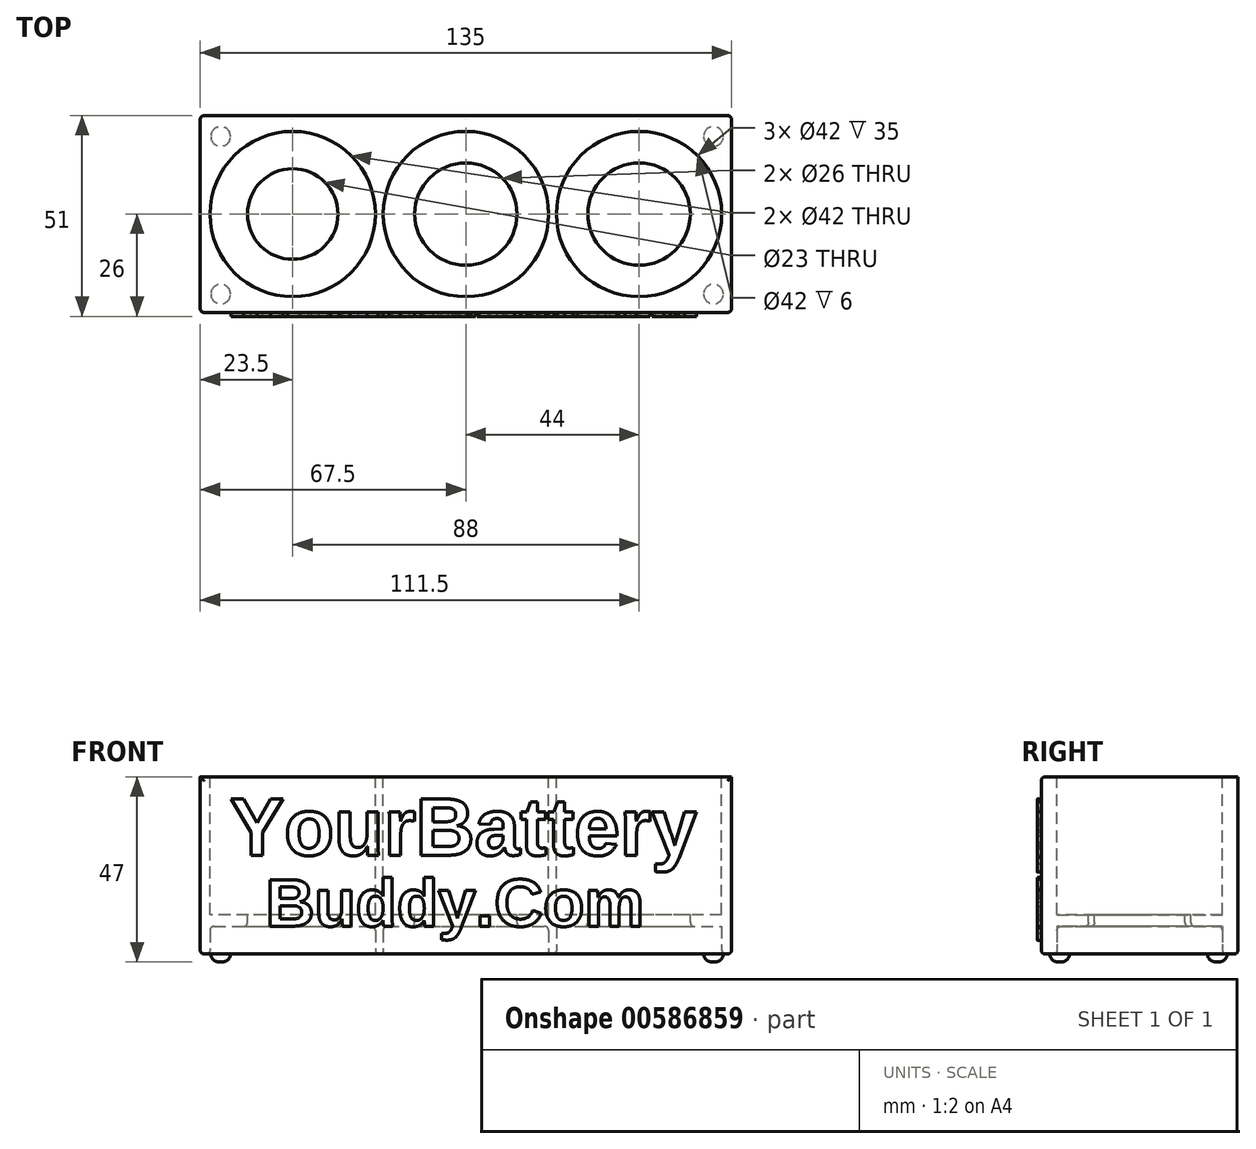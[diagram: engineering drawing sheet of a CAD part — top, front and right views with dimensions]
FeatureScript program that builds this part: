
annotation { "Feature Type Name" : "Feature", "Feature Type Description" : "" }
export const myFeature = defineFeature(function(context is Context, id is Id, definition is map)
    precondition{}
    {
        {
            var Q0;
            Q0=qCreatedBy(makeId("Top.planeOp"),FACE);
            var sketch = newSketch(context, id + "F0", { "sketchPlane" : qUnion([Q0])});
            skLineSegment(sketch, "E0.bottom", {"start": v(-67.5, -25) * mm, "end": v(67.5, -25) * mm});
            skLineSegment(sketch, "E0.top", {"start": v(-67.5, 25) * mm, "end": v(67.5, 25) * mm});
            skLineSegment(sketch, "E0.left", {"start": v(-67.5, -25) * mm, "end": v(-67.5, 25) * mm});
            skLineSegment(sketch, "E0.right", {"start": v(67.5, -25) * mm, "end": v(67.5, 25) * mm});
            skPoint(sketch, "E0.middle", {"position": v(0, 0) * mm});
            skSolve(sketch);
        }
        {
            var Q0;
            Q0 = qSketchRegion(id + "F0", true);
            extrude(context, id + "F1", {"entities" : qUnion([Q0]), "endBound" : BoundingType.SYMMETRIC, "depth" : 45 * mm, "offsetDistance" : 25 * mm});
        }
        {
            var Q0;
            Q0=makeQuery(id+"F1.opExtrude","CAP_FACE",FACE,{"disambiguationData":[OSD([sQuery(id+"F0.wireOp",EDGE,"E0.bottom"),sQuery(id+"F0.wireOp",EDGE,"E0.top"),sQuery(id+"F0.wireOp",EDGE,"E0.left"),sQuery(id+"F0.wireOp",EDGE,"E0.right")])],"isStart":false});
            var sketch = newSketch(context, id + "F2", { "sketchPlane" : qUnion([Q0])});
            skCircle(sketch, "E1", {"center": v(-44, 0) * mm, "radius": 21 * mm});
            skCircle(sketch, "E2", {"center": v(0, 0) * mm, "radius": 21 * mm});
            skCircle(sketch, "E3", {"center": v(44, 0) * mm, "radius": 21 * mm});
            skSolve(sketch);
        }
        {
            var Q0;
            Q0 = qSketchRegion(id + "F2", true);
            extrude(context, id + "F3", {"entities" : qUnion([Q0]), "operationType" : NewBodyOperationType.REMOVE, "oppositeDirection" : true, "depth" : 35 * mm, "offsetDistance" : 25 * mm});
        }
        {
            var Q0;
            Q0=makeQuery(id+"F3.boolean.opBoolean","COPY",FACE,{"derivedFrom":makeQuery(id+"F3.opExtrude","CAP_FACE",FACE,{"disambiguationData":[OSD([sQuery(id+"F2.wireOp",EDGE,"E1")])],"isStart":false})});
            var sketch = newSketch(context, id + "F4", { "sketchPlane" : qUnion([Q0])});
            skCircle(sketch, "E4", {"center": v(-44, 0) * mm, "radius": 13 * mm});
            skSolve(sketch);
        }
        {
            var Q0;
            Q0 = qSketchRegion(id + "F4", true);
            extrude(context, id + "F5", {"entities" : qUnion([Q0]), "operationType" : NewBodyOperationType.REMOVE, "endBound" : BoundingType.THROUGH_ALL, "depth" : 25 * mm, "offsetDistance" : 25 * mm});
        }
        {
            var Q0;
            Q0=makeQuery(id+"F3.boolean.opBoolean","COPY",FACE,{"derivedFrom":makeQuery(id+"F3.opExtrude","CAP_FACE",FACE,{"disambiguationData":[OSD([sQuery(id+"F2.wireOp",EDGE,"E2")])],"isStart":false})});
            var sketch = newSketch(context, id + "F6", { "sketchPlane" : qUnion([Q0])});
            skCircle(sketch, "E5", {"center": v(0, 0) * mm, "radius": 13 * mm});
            skSolve(sketch);
        }
        {
            var Q0;
            Q0 = qSketchRegion(id + "F6", true);
            extrude(context, id + "F7", {"entities" : qUnion([Q0]), "operationType" : NewBodyOperationType.REMOVE, "endBound" : BoundingType.THROUGH_ALL, "oppositeDirection" : true, "depth" : 25 * mm, "offsetDistance" : 25 * mm});
        }
        {
            var Q0;
            Q0=makeQuery(id+"F3.boolean.opBoolean","COPY",FACE,{"derivedFrom":makeQuery(id+"F3.opExtrude","CAP_FACE",FACE,{"disambiguationData":[OSD([sQuery(id+"F2.wireOp",EDGE,"E3")])],"isStart":false})});
            var sketch = newSketch(context, id + "F8", { "sketchPlane" : qUnion([Q0])});
            skCircle(sketch, "E6", {"center": v(44, 0) * mm, "radius": 13 * mm});
            skSolve(sketch);
        }
        {
            var Q0;
            Q0 = qSketchRegion(id + "F8", true);
            extrude(context, id + "F9", {"entities" : qUnion([Q0]), "operationType" : NewBodyOperationType.REMOVE, "endBound" : BoundingType.THROUGH_ALL, "oppositeDirection" : true, "depth" : 25 * mm, "offsetDistance" : 25 * mm});
        }
        {
            var Q0;
            Q0=makeQuery(id+"F3.boolean.opBoolean","COPY",FACE,{"derivedFrom":makeQuery(id+"F3.opExtrude","CAP_FACE",FACE,{"disambiguationData":[OSD([sQuery(id+"F2.wireOp",EDGE,"E1")])],"isStart":false})});
            var sketch = newSketch(context, id + "F10", { "sketchPlane" : qUnion([Q0])});
            skCircle(sketch, "E7", {"center": v(-44, 0) * mm, "radius": 11.5 * mm});
            skSolve(sketch);
        }
        {
            var Q0;
            Q0 = qSketchRegion(id + "F10", true);
            extrude(context, id + "F11", {"entities" : qUnion([Q0]), "operationType" : NewBodyOperationType.REMOVE, "endBound" : BoundingType.THROUGH_ALL, "oppositeDirection" : true, "depth" : 25 * mm, "offsetDistance" : 25 * mm});
        }
        {
            var Q0;
            Q0=makeQuery(id+"F1.opExtrude","CAP_FACE",FACE,{"disambiguationData":[OSD([sQuery(id+"F0.wireOp",EDGE,"E0.bottom"),sQuery(id+"F0.wireOp",EDGE,"E0.top"),sQuery(id+"F0.wireOp",EDGE,"E0.left"),sQuery(id+"F0.wireOp",EDGE,"E0.right")])],"isStart":true});
            var sketch = newSketch(context, id + "F12", { "sketchPlane" : qUnion([Q0])});
            skCircle(sketch, "E8", {"center": v(0, 0) * mm, "radius": 21 * mm});
            skSolve(sketch);
        }
        {
            var Q0;
            Q0 = qSketchRegion(id + "F12", true);
            extrude(context, id + "F13", {"entities" : qUnion([Q0]), "operationType" : NewBodyOperationType.REMOVE, "oppositeDirection" : true, "depth" : 7 * mm, "offsetDistance" : 25 * mm});
        }
        {
            var Q0;
            Q0=makeQuery(id+"F1.opExtrude","CAP_FACE",FACE,{"disambiguationData":[OSD([sQuery(id+"F0.wireOp",EDGE,"E0.bottom"),sQuery(id+"F0.wireOp",EDGE,"E0.top"),sQuery(id+"F0.wireOp",EDGE,"E0.left"),sQuery(id+"F0.wireOp",EDGE,"E0.right")])],"isStart":true});
            var sketch = newSketch(context, id + "F14", { "sketchPlane" : qUnion([Q0])});
            skCircle(sketch, "E9", {"center": v(-44, 0) * mm, "radius": 21 * mm});
            skSolve(sketch);
        }
        {
            var Q0;
            Q0 = qSketchRegion(id + "F14", true);
            extrude(context, id + "F15", {"entities" : qUnion([Q0]), "operationType" : NewBodyOperationType.REMOVE, "oppositeDirection" : true, "depth" : 7 * mm, "offsetDistance" : 25 * mm});
        }
        {
            var Q0;
            Q0=makeQuery(id+"F1.opExtrude","CAP_FACE",FACE,{"disambiguationData":[OSD([sQuery(id+"F0.wireOp",EDGE,"E0.bottom"),sQuery(id+"F0.wireOp",EDGE,"E0.top"),sQuery(id+"F0.wireOp",EDGE,"E0.left"),sQuery(id+"F0.wireOp",EDGE,"E0.right")])],"isStart":true});
            var sketch = newSketch(context, id + "F16", { "sketchPlane" : qUnion([Q0])});
            skCircle(sketch, "E10", {"center": v(44, 0) * mm, "radius": 21 * mm});
            skSolve(sketch);
        }
        {
            var Q0;
            Q0 = qSketchRegion(id + "F16", true);
            extrude(context, id + "F17", {"entities" : qUnion([Q0]), "operationType" : NewBodyOperationType.REMOVE, "oppositeDirection" : true, "depth" : 7 * mm, "offsetDistance" : 25 * mm});
        }
        {
            var Q0;
            Q0=makeQuery(id+"F1.opExtrude","CAP_FACE",FACE,{"disambiguationData":[OSD([sQuery(id+"F0.wireOp",EDGE,"E0.bottom"),sQuery(id+"F0.wireOp",EDGE,"E0.top"),sQuery(id+"F0.wireOp",EDGE,"E0.left"),sQuery(id+"F0.wireOp",EDGE,"E0.right")])],"isStart":true});
            var Q1;
            Q1=makeQuery(id+"F15.boolean.opBoolean","INTERSECT",EDGE,{"derivedFrom":[makeQuery(id+"F11.boolean.opBoolean","COPY",FACE,{"derivedFrom":makeQuery(id+"F11.opExtrude","SWEPT_FACE",FACE,{"disambiguationData":[OSD([sQuery(id+"F10.wireOp",EDGE,"E7")])]})}),makeQuery(id+"F15.opExtrude","CAP_FACE",FACE,{"disambiguationData":[OSD([sQuery(id+"F14.wireOp",EDGE,"E9")])],"isStart":false})]});
            var Q2;
            Q2=makeQuery(id+"F7.boolean.opBoolean","COPY",EDGE,{"derivedFrom":makeQuery(id+"F7.opExtrude","CAP_EDGE",EDGE,{"disambiguationData":[OSD([sQuery(id+"F6.wireOp",EDGE,"E5")])],"isStart":true})});
            var Q3;
            Q3=makeQuery(id+"F17.boolean.opBoolean","INTERSECT",EDGE,{"derivedFrom":[makeQuery(id+"F9.boolean.opBoolean","COPY",FACE,{"derivedFrom":makeQuery(id+"F9.opExtrude","SWEPT_FACE",FACE,{"disambiguationData":[OSD([sQuery(id+"F8.wireOp",EDGE,"E6")])]})}),makeQuery(id+"F17.opExtrude","CAP_FACE",FACE,{"disambiguationData":[OSD([sQuery(id+"F16.wireOp",EDGE,"E10")])],"isStart":false})]});
            var Q4;
            Q4=makeQuery(id+"F1.opExtrude","SWEPT_EDGE",EDGE,{"disambiguationData":[OSD([sQuery(id+"F0.wireOp",EDGE,"E0.bottom"),sQuery(id+"F0.wireOp",EDGE,"E0.left")])]});
            var Q5;
            Q5=makeQuery(id+"F1.opExtrude","CAP_EDGE",EDGE,{"disambiguationData":[OSD([sQuery(id+"F0.wireOp",EDGE,"E0.bottom")])],"isStart":false});
            var Q6;
            Q6=makeQuery(id+"F1.opExtrude","SWEPT_EDGE",EDGE,{"disambiguationData":[OSD([sQuery(id+"F0.wireOp",EDGE,"E0.bottom"),sQuery(id+"F0.wireOp",EDGE,"E0.right")])]});
            var Q7;
            Q7=makeQuery(id+"F3.boolean.opBoolean","COPY",EDGE,{"derivedFrom":makeQuery(id+"F3.opExtrude","CAP_EDGE",EDGE,{"disambiguationData":[OSD([sQuery(id+"F2.wireOp",EDGE,"E3")])],"isStart":true})});
            var Q8;
            Q8=makeQuery(id+"F3.boolean.opBoolean","COPY",EDGE,{"derivedFrom":makeQuery(id+"F3.opExtrude","CAP_EDGE",EDGE,{"disambiguationData":[OSD([sQuery(id+"F2.wireOp",EDGE,"E2")])],"isStart":true})});
            var Q9;
            Q9=makeQuery(id+"F3.boolean.opBoolean","COPY",EDGE,{"derivedFrom":makeQuery(id+"F3.opExtrude","CAP_EDGE",EDGE,{"disambiguationData":[OSD([sQuery(id+"F2.wireOp",EDGE,"E1")])],"isStart":true})});
            var Q10;
            Q10=makeQuery(id+"F1.opExtrude","SWEPT_EDGE",EDGE,{"disambiguationData":[OSD([sQuery(id+"F0.wireOp",EDGE,"E0.top"),sQuery(id+"F0.wireOp",EDGE,"E0.left")])]});
            var Q11;
            Q11=makeQuery(id+"F1.opExtrude","SWEPT_EDGE",EDGE,{"disambiguationData":[OSD([sQuery(id+"F0.wireOp",EDGE,"E0.top"),sQuery(id+"F0.wireOp",EDGE,"E0.right")])]});
            var Q12;
            Q12=makeQuery(id+"F9.boolean.opBoolean","COPY",EDGE,{"derivedFrom":makeQuery(id+"F9.opExtrude","CAP_EDGE",EDGE,{"disambiguationData":[OSD([sQuery(id+"F8.wireOp",EDGE,"E6")])],"isStart":true})});
            var Q13;
            Q13=makeQuery(id+"F13.boolean.opBoolean","INTERSECT",EDGE,{"derivedFrom":[makeQuery(id+"F7.boolean.opBoolean","COPY",FACE,{"derivedFrom":makeQuery(id+"F7.opExtrude","SWEPT_FACE",FACE,{"disambiguationData":[OSD([sQuery(id+"F6.wireOp",EDGE,"E5")])]})}),makeQuery(id+"F13.opExtrude","CAP_FACE",FACE,{"disambiguationData":[OSD([sQuery(id+"F12.wireOp",EDGE,"E8")])],"isStart":false})]});
            var Q14;
            Q14=makeQuery(id+"F13.boolean.opBoolean","COPY",EDGE,{"derivedFrom":makeQuery(id+"F13.opExtrude","CAP_EDGE",EDGE,{"disambiguationData":[OSD([sQuery(id+"F12.wireOp",EDGE,"E8")])],"isStart":false})});
            var Q15;
            Q15=makeQuery(id+"F15.boolean.opBoolean","COPY",EDGE,{"derivedFrom":makeQuery(id+"F15.opExtrude","CAP_EDGE",EDGE,{"disambiguationData":[OSD([sQuery(id+"F14.wireOp",EDGE,"E9")])],"isStart":false})});
            var Q16;
            Q16=makeQuery(id+"F11.boolean.opBoolean","COPY",EDGE,{"derivedFrom":makeQuery(id+"F11.opExtrude","CAP_EDGE",EDGE,{"disambiguationData":[OSD([sQuery(id+"F10.wireOp",EDGE,"E7")])],"isStart":true})});
            fillet(context, id + "F18", {"entities" : qUnion([Q0, Q1, Q2, Q3, Q4, Q5, Q6, Q7, Q8, Q9, Q10, Q11, Q12, Q13, Q14, Q15, Q16]), "radius" : 1 * mm, "tangentPropagation" : true, "allowEdgeOverflow" : false});
        }
        {
            var Q0;
            Q0=makeQuery(id+"F1.opExtrude","CAP_FACE",FACE,{"disambiguationData":[OSD([sQuery(id+"F0.wireOp",EDGE,"E0.bottom"),sQuery(id+"F0.wireOp",EDGE,"E0.top"),sQuery(id+"F0.wireOp",EDGE,"E0.left"),sQuery(id+"F0.wireOp",EDGE,"E0.right")])],"isStart":true});
            var sketch = newSketch(context, id + "F19", { "sketchPlane" : qUnion([Q0])});
            skCircle(sketch, "E11", {"center": v(-62.29, -19.71) * mm, "radius": 2.5 * mm});
            skCircle(sketch, "E12", {"center": v(-62.29, 20.34) * mm, "radius": 2.5 * mm});
            skCircle(sketch, "E13", {"center": v(62.9, 20.34) * mm, "radius": 2.5 * mm});
            skCircle(sketch, "E14", {"center": v(62.9, -19.71) * mm, "radius": 2.5 * mm});
            skSolve(sketch);
        }
        {
            var Q0;
            Q0 = qSketchRegion(id + "F19", true);
            extrude(context, id + "F20", {"entities" : qUnion([Q0]), "operationType" : NewBodyOperationType.ADD, "depth" : 2 * mm, "offsetDistance" : 25 * mm});
        }
        {
            var Q0;
            Q0=makeQuery(id+"F20.opExtrude","CAP_EDGE",EDGE,{"disambiguationData":[OSD([sQuery(id+"F19.wireOp",EDGE,"E12")])],"isStart":false});
            var Q1;
            Q1=makeQuery(id+"F20.opExtrude","CAP_EDGE",EDGE,{"disambiguationData":[OSD([sQuery(id+"F19.wireOp",EDGE,"E11")])],"isStart":false});
            var Q2;
            Q2=makeQuery(id+"F20.opExtrude","CAP_EDGE",EDGE,{"disambiguationData":[OSD([sQuery(id+"F19.wireOp",EDGE,"E14")])],"isStart":false});
            var Q3;
            Q3=makeQuery(id+"F20.opExtrude","CAP_EDGE",EDGE,{"disambiguationData":[OSD([sQuery(id+"F19.wireOp",EDGE,"E13")])],"isStart":false});
            fillet(context, id + "F21", {"entities" : qUnion([Q0, Q1, Q2, Q3]), "radius" : 2 * mm, "tangentPropagation" : true, "allowEdgeOverflow" : false});
        }
        {
            var Q0;
            Q0=makeQuery(id+"F1.opExtrude","SWEPT_FACE",FACE,{"disambiguationData":[OSD([sQuery(id+"F0.wireOp",EDGE,"E0.bottom")])]});
            var sketch = newSketch(context, id + "F22", { "sketchPlane" : qUnion([Q0])});
            skText(sketch, "E15", { "text": "YourBattery", "fontName": "Arimo-Bold.ttf"});
            skText(sketch, "E16", { "text": "Buddy.Com", "fontName": "Arimo-Bold.ttf"});
            const initialGuessF22  = {"E15": [-0.06, 0.0026, 1, 0, 0.01493], "E16": [-0.05083, -0.01543, 1, 0, 0.01234]};
            skSetInitialGuess(sketch, initialGuessF22);
            skSolve(sketch);
        }
        {
            var Q0;
            Q0 = qSketchRegion(id + "F22", true);
            extrude(context, id + "F23", {"entities" : qUnion([Q0]), "operationType" : NewBodyOperationType.ADD, "depth" : 1 * mm, "offsetDistance" : 25 * mm});
        }
    });
